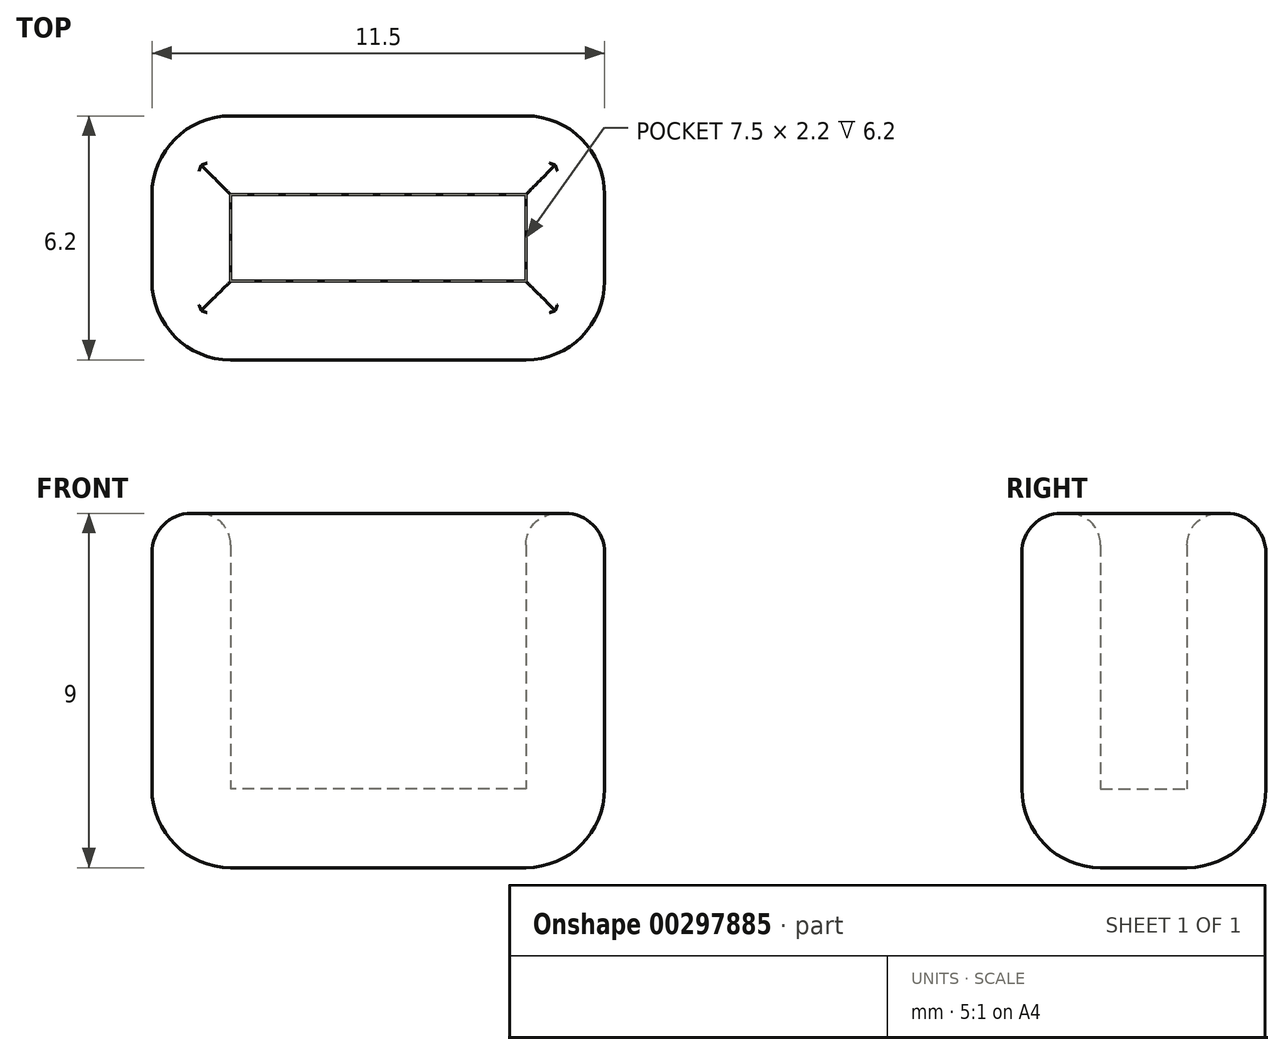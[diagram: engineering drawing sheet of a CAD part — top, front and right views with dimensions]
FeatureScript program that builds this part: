
annotation { "Feature Type Name" : "Feature", "Feature Type Description" : "" }
export const myFeature = defineFeature(function(context is Context, id is Id, definition is map)
    precondition{}
    {
        {
            var Q0;
            Q0=qCreatedBy(makeId("Top.planeOp"),FACE);
            var sketch = newSketch(context, id + "F0", { "sketchPlane" : qUnion([Q0])});
            skLineSegment(sketch, "E0.bottom", {"start": v(3.75, -1.1) * mm, "end": v(-3.75, -1.1) * mm});
            skLineSegment(sketch, "E0.top", {"start": v(3.75, 1.1) * mm, "end": v(-3.75, 1.1) * mm});
            skLineSegment(sketch, "E0.left", {"start": v(3.75, -1.1) * mm, "end": v(3.75, 1.1) * mm});
            skLineSegment(sketch, "E0.right", {"start": v(-3.75, -1.1) * mm, "end": v(-3.75, 1.1) * mm});
            skPoint(sketch, "E0.middle", {"position": v(0, 0) * mm});
            skLineSegment(sketch, "E1.0", {"start": v(5.75, -3.1) * mm, "end": v(-5.75, -3.1) * mm});
            skLineSegment(sketch, "E1.1", {"start": v(5.75, -3.1) * mm, "end": v(5.75, 3.1) * mm});
            skLineSegment(sketch, "E1.2", {"start": v(5.75, 3.1) * mm, "end": v(-5.75, 3.1) * mm});
            skLineSegment(sketch, "E1.3", {"start": v(-5.75, -3.1) * mm, "end": v(-5.75, 3.1) * mm});
            skSolve(sketch);
        }
        {
            var Q0;
            Q0=makeQuery(id+"F0.imprint","IMPRINT",FACE,{"disambiguationData":[TD([[makeQuery(id+"F0.imprint","IMPRINT",EDGE,{"derivedFrom":sQuery(id+"F0.wireOp",EDGE,"E0.bottom")}),1.0]])]});
            extrude(context, id + "F1", {"entities" : qUnion([Q0]), "depth" : 7 * mm});
        }
        {
            var Q0;
            Q0=makeQuery(id+"F1.opExtrude","CAP_FACE",FACE,{"disambiguationData":[OSD([sQuery(id+"F0.wireOp",EDGE,"E0.bottom"),sQuery(id+"F0.wireOp",EDGE,"E0.top"),sQuery(id+"F0.wireOp",EDGE,"E0.left"),sQuery(id+"F0.wireOp",EDGE,"E0.right"),sQuery(id+"F0.wireOp",EDGE,"E1.0"),sQuery(id+"F0.wireOp",EDGE,"E1.1"),sQuery(id+"F0.wireOp",EDGE,"E1.2"),sQuery(id+"F0.wireOp",EDGE,"E1.3")])],"isStart":true});
            var sketch = newSketch(context, id + "F2", { "sketchPlane" : qUnion([Q0])});
            skPoint(sketch, "E2.0", {"position": v(5.75, 0) * mm});
            skLineSegment(sketch, "E3.0", {"start": v(5.75, 3.1) * mm, "end": v(5.75, -3.1) * mm});
            skLineSegment(sketch, "E4.0", {"start": v(5.75, 3.1) * mm, "end": v(-5.75, 3.1) * mm});
            skLineSegment(sketch, "E5.0", {"start": v(5.75, -3.1) * mm, "end": v(-5.75, -3.1) * mm});
            skLineSegment(sketch, "E6.0", {"start": v(-5.75, 3.1) * mm, "end": v(-5.75, -3.1) * mm});
            skSolve(sketch);
        }
        {
            var Q0;
            Q0 = qSketchRegion(id + "F2", true);
            extrude(context, id + "F3", {"entities" : qUnion([Q0]), "operationType" : NewBodyOperationType.ADD, "depth" : 2 * mm});
        }
        {
            var Q0;
            Q0=makeQuery(id+"F3.opExtrude","CAP_FACE",FACE,{"disambiguationData":[OSD([sQuery(id+"F2.wireOp",EDGE,"E3.0"),sQuery(id+"F2.wireOp",EDGE,"E4.0"),sQuery(id+"F2.wireOp",EDGE,"E5.0"),sQuery(id+"F2.wireOp",EDGE,"E6.0")])],"isStart":false});
            var Q1;
            Q1=makeQuery(id+"F3.boolean.opBoolean","MERGE",EDGE,{"derivedFrom":[makeQuery(id+"F1.opExtrude","SWEPT_EDGE",EDGE,{"disambiguationData":[OSD([sQuery(id+"F0.wireOp",EDGE,"E1.0"),sQuery(id+"F0.wireOp",EDGE,"E1.1")])]}),makeQuery(id+"F3.opExtrude","SWEPT_EDGE",EDGE,{"disambiguationData":[OSD([sQuery(id+"F2.wireOp",EDGE,"E3.0"),sQuery(id+"F2.wireOp",EDGE,"E4.0")])]})]});
            var Q2;
            Q2=makeQuery(id+"F3.boolean.opBoolean","MERGE",EDGE,{"derivedFrom":[makeQuery(id+"F1.opExtrude","SWEPT_EDGE",EDGE,{"disambiguationData":[OSD([sQuery(id+"F0.wireOp",EDGE,"E1.1"),sQuery(id+"F0.wireOp",EDGE,"E1.2")])]}),makeQuery(id+"F3.opExtrude","SWEPT_EDGE",EDGE,{"disambiguationData":[OSD([sQuery(id+"F2.wireOp",EDGE,"E3.0"),sQuery(id+"F2.wireOp",EDGE,"E5.0")])]})]});
            var Q3;
            Q3=makeQuery(id+"F3.boolean.opBoolean","MERGE",EDGE,{"derivedFrom":[makeQuery(id+"F1.opExtrude","SWEPT_EDGE",EDGE,{"disambiguationData":[OSD([sQuery(id+"F0.wireOp",EDGE,"E1.0"),sQuery(id+"F0.wireOp",EDGE,"E1.3")])]}),makeQuery(id+"F3.opExtrude","SWEPT_EDGE",EDGE,{"disambiguationData":[OSD([sQuery(id+"F2.wireOp",EDGE,"E4.0"),sQuery(id+"F2.wireOp",EDGE,"E6.0")])]})]});
            var Q4;
            Q4=makeQuery(id+"F3.boolean.opBoolean","MERGE",EDGE,{"derivedFrom":[makeQuery(id+"F1.opExtrude","SWEPT_EDGE",EDGE,{"disambiguationData":[OSD([sQuery(id+"F0.wireOp",EDGE,"E1.2"),sQuery(id+"F0.wireOp",EDGE,"E1.3")])]}),makeQuery(id+"F3.opExtrude","SWEPT_EDGE",EDGE,{"disambiguationData":[OSD([sQuery(id+"F2.wireOp",EDGE,"E5.0"),sQuery(id+"F2.wireOp",EDGE,"E6.0")])]})]});
            fillet(context, id + "F4", {"entities" : qUnion([Q0, Q1, Q2, Q3, Q4]), "radius" : 2 * mm, "tangentPropagation" : true, "allowEdgeOverflow" : false});
        }
        {
            var Q0;
            Q0=makeQuery(id+"F1.opExtrude","CAP_EDGE",EDGE,{"disambiguationData":[OSD([sQuery(id+"F0.wireOp",EDGE,"E0.bottom")])],"isStart":false});
            var Q1;
            Q1=makeQuery(id+"F1.opExtrude","CAP_EDGE",EDGE,{"disambiguationData":[OSD([sQuery(id+"F0.wireOp",EDGE,"E0.left")])],"isStart":false});
            var Q2;
            Q2=makeQuery(id+"F1.opExtrude","CAP_EDGE",EDGE,{"disambiguationData":[OSD([sQuery(id+"F0.wireOp",EDGE,"E0.right")])],"isStart":false});
            var Q3;
            Q3=makeQuery(id+"F1.opExtrude","CAP_EDGE",EDGE,{"disambiguationData":[OSD([sQuery(id+"F0.wireOp",EDGE,"E0.top")])],"isStart":false});
            fillet(context, id + "F5", {"entities" : qUnion([Q0, Q1, Q2, Q3]), "radius" : .8 * mm, "tangentPropagation" : true, "allowEdgeOverflow" : false});
        }
        {
            var Q0;
            Q0=makeQuery(id+"F1.opExtrude","CAP_EDGE",EDGE,{"disambiguationData":[OSD([sQuery(id+"F0.wireOp",EDGE,"E1.1")])],"isStart":false});
            var Q1;
            Q1=makeQuery(id+"F1.opExtrude","CAP_EDGE",EDGE,{"disambiguationData":[OSD([sQuery(id+"F0.wireOp",EDGE,"E1.2")])],"isStart":false});
            var Q2;
            {var subQ0=sQuery(id+"F0.wireOp",EDGE,"E1.2");var subQ1=sQuery(id+"F0.wireOp",EDGE,"E1.1");Q2=makeQuery(id+"F4.opFillet","BLEND_EDGE",EDGE,{"blendedFrom":[makeQuery(id+"F3.boolean.opBoolean","MERGE",EDGE,{"derivedFrom":[makeQuery(id+"F1.opExtrude","SWEPT_EDGE",EDGE,{"disambiguationData":[OSD([subQ1,subQ0])]}),makeQuery(id+"F3.opExtrude","SWEPT_EDGE",EDGE,{"disambiguationData":[OSD([sQuery(id+"F2.wireOp",EDGE,"E3.0"),sQuery(id+"F2.wireOp",EDGE,"E5.0")])]})]}),makeQuery(id+"F1.opExtrude","CAP_FACE",FACE,{"disambiguationData":[OSD([sQuery(id+"F0.wireOp",EDGE,"E0.bottom"),sQuery(id+"F0.wireOp",EDGE,"E0.top"),sQuery(id+"F0.wireOp",EDGE,"E0.left"),sQuery(id+"F0.wireOp",EDGE,"E0.right"),sQuery(id+"F0.wireOp",EDGE,"E1.0"),subQ1,subQ0,sQuery(id+"F0.wireOp",EDGE,"E1.3")])],"isStart":false})],"blendedInto":[makeQuery(id+"F1.opExtrude","CAP_FACE",FACE,{"disambiguationData":[OSD([sQuery(id+"F0.wireOp",EDGE,"E0.bottom"),sQuery(id+"F0.wireOp",EDGE,"E0.top"),sQuery(id+"F0.wireOp",EDGE,"E0.left"),sQuery(id+"F0.wireOp",EDGE,"E0.right"),sQuery(id+"F0.wireOp",EDGE,"E1.0"),subQ1,subQ0,sQuery(id+"F0.wireOp",EDGE,"E1.3")])],"isStart":false})]});}
            var Q3;
            {var subQ0=sQuery(id+"F0.wireOp",EDGE,"E1.3");var subQ1=sQuery(id+"F0.wireOp",EDGE,"E1.2");Q3=makeQuery(id+"F4.opFillet","BLEND_EDGE",EDGE,{"blendedFrom":[makeQuery(id+"F3.boolean.opBoolean","MERGE",EDGE,{"derivedFrom":[makeQuery(id+"F1.opExtrude","SWEPT_EDGE",EDGE,{"disambiguationData":[OSD([subQ1,subQ0])]}),makeQuery(id+"F3.opExtrude","SWEPT_EDGE",EDGE,{"disambiguationData":[OSD([sQuery(id+"F2.wireOp",EDGE,"E5.0"),sQuery(id+"F2.wireOp",EDGE,"E6.0")])]})]}),makeQuery(id+"F1.opExtrude","CAP_FACE",FACE,{"disambiguationData":[OSD([sQuery(id+"F0.wireOp",EDGE,"E0.bottom"),sQuery(id+"F0.wireOp",EDGE,"E0.top"),sQuery(id+"F0.wireOp",EDGE,"E0.left"),sQuery(id+"F0.wireOp",EDGE,"E0.right"),sQuery(id+"F0.wireOp",EDGE,"E1.0"),sQuery(id+"F0.wireOp",EDGE,"E1.1"),subQ1,subQ0])],"isStart":false})],"blendedInto":[makeQuery(id+"F1.opExtrude","CAP_FACE",FACE,{"disambiguationData":[OSD([sQuery(id+"F0.wireOp",EDGE,"E0.bottom"),sQuery(id+"F0.wireOp",EDGE,"E0.top"),sQuery(id+"F0.wireOp",EDGE,"E0.left"),sQuery(id+"F0.wireOp",EDGE,"E0.right"),sQuery(id+"F0.wireOp",EDGE,"E1.0"),sQuery(id+"F0.wireOp",EDGE,"E1.1"),subQ1,subQ0])],"isStart":false})]});}
            var Q4;
            Q4=makeQuery(id+"F1.opExtrude","CAP_EDGE",EDGE,{"disambiguationData":[OSD([sQuery(id+"F0.wireOp",EDGE,"E1.3")])],"isStart":false});
            var Q5;
            {var subQ0=sQuery(id+"F0.wireOp",EDGE,"E1.1");var subQ1=sQuery(id+"F0.wireOp",EDGE,"E1.0");Q5=makeQuery(id+"F4.opFillet","BLEND_EDGE",EDGE,{"blendedFrom":[makeQuery(id+"F3.boolean.opBoolean","MERGE",EDGE,{"derivedFrom":[makeQuery(id+"F1.opExtrude","SWEPT_EDGE",EDGE,{"disambiguationData":[OSD([subQ1,subQ0])]}),makeQuery(id+"F3.opExtrude","SWEPT_EDGE",EDGE,{"disambiguationData":[OSD([sQuery(id+"F2.wireOp",EDGE,"E3.0"),sQuery(id+"F2.wireOp",EDGE,"E4.0")])]})]}),makeQuery(id+"F1.opExtrude","CAP_FACE",FACE,{"disambiguationData":[OSD([sQuery(id+"F0.wireOp",EDGE,"E0.bottom"),sQuery(id+"F0.wireOp",EDGE,"E0.top"),sQuery(id+"F0.wireOp",EDGE,"E0.left"),sQuery(id+"F0.wireOp",EDGE,"E0.right"),subQ1,subQ0,sQuery(id+"F0.wireOp",EDGE,"E1.2"),sQuery(id+"F0.wireOp",EDGE,"E1.3")])],"isStart":false})],"blendedInto":[makeQuery(id+"F1.opExtrude","CAP_FACE",FACE,{"disambiguationData":[OSD([sQuery(id+"F0.wireOp",EDGE,"E0.bottom"),sQuery(id+"F0.wireOp",EDGE,"E0.top"),sQuery(id+"F0.wireOp",EDGE,"E0.left"),sQuery(id+"F0.wireOp",EDGE,"E0.right"),subQ1,subQ0,sQuery(id+"F0.wireOp",EDGE,"E1.2"),sQuery(id+"F0.wireOp",EDGE,"E1.3")])],"isStart":false})]});}
            var Q6;
            {var subQ0=sQuery(id+"F0.wireOp",EDGE,"E1.3");var subQ1=sQuery(id+"F0.wireOp",EDGE,"E1.0");Q6=makeQuery(id+"F4.opFillet","BLEND_EDGE",EDGE,{"blendedFrom":[makeQuery(id+"F3.boolean.opBoolean","MERGE",EDGE,{"derivedFrom":[makeQuery(id+"F1.opExtrude","SWEPT_EDGE",EDGE,{"disambiguationData":[OSD([subQ1,subQ0])]}),makeQuery(id+"F3.opExtrude","SWEPT_EDGE",EDGE,{"disambiguationData":[OSD([sQuery(id+"F2.wireOp",EDGE,"E4.0"),sQuery(id+"F2.wireOp",EDGE,"E6.0")])]})]}),makeQuery(id+"F1.opExtrude","CAP_FACE",FACE,{"disambiguationData":[OSD([sQuery(id+"F0.wireOp",EDGE,"E0.bottom"),sQuery(id+"F0.wireOp",EDGE,"E0.top"),sQuery(id+"F0.wireOp",EDGE,"E0.left"),sQuery(id+"F0.wireOp",EDGE,"E0.right"),subQ1,sQuery(id+"F0.wireOp",EDGE,"E1.1"),sQuery(id+"F0.wireOp",EDGE,"E1.2"),subQ0])],"isStart":false})],"blendedInto":[makeQuery(id+"F1.opExtrude","CAP_FACE",FACE,{"disambiguationData":[OSD([sQuery(id+"F0.wireOp",EDGE,"E0.bottom"),sQuery(id+"F0.wireOp",EDGE,"E0.top"),sQuery(id+"F0.wireOp",EDGE,"E0.left"),sQuery(id+"F0.wireOp",EDGE,"E0.right"),subQ1,sQuery(id+"F0.wireOp",EDGE,"E1.1"),sQuery(id+"F0.wireOp",EDGE,"E1.2"),subQ0])],"isStart":false})]});}
            var Q7;
            Q7=makeQuery(id+"F1.opExtrude","CAP_EDGE",EDGE,{"disambiguationData":[OSD([sQuery(id+"F0.wireOp",EDGE,"E1.0")])],"isStart":false});
            fillet(context, id + "F6", {"entities" : qUnion([Q0, Q1, Q2, Q3, Q4, Q5, Q6, Q7]), "radius" : 1 * mm, "tangentPropagation" : true, "allowEdgeOverflow" : false});
        }
    });
